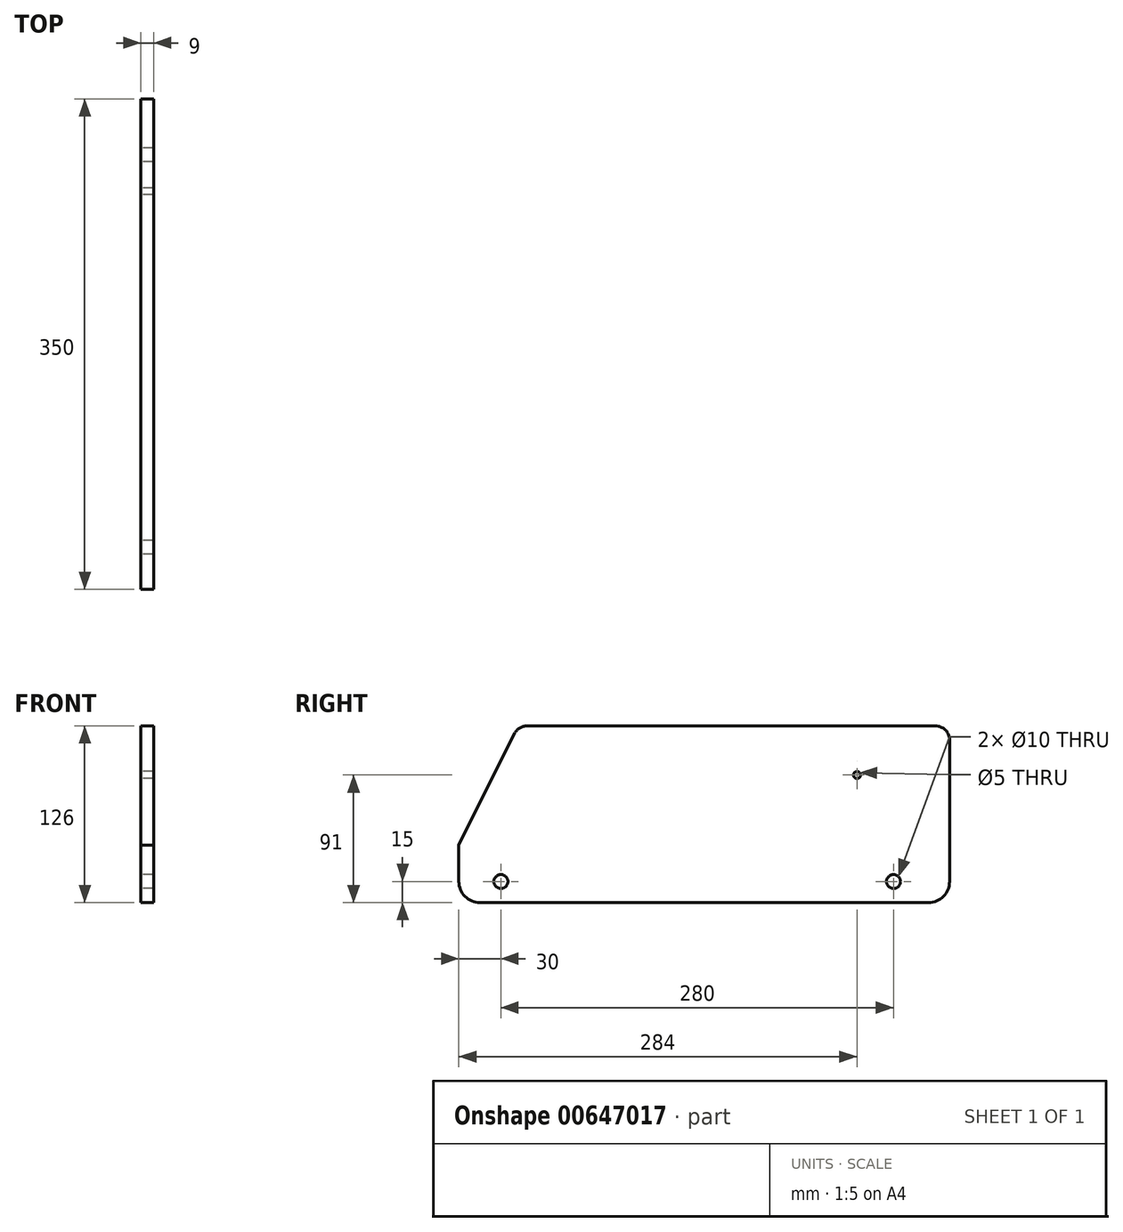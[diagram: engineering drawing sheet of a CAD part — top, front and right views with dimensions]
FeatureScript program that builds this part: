
annotation { "Feature Type Name" : "Feature", "Feature Type Description" : "" }
export const myFeature = defineFeature(function(context is Context, id is Id, definition is map)
    precondition{}
    {
        {
            var Q0;
            Q0=qCreatedBy(makeId("Right.planeOp"),FACE);
            var sketch = newSketch(context, id + "F0", { "sketchPlane" : qUnion([Q0])});
            skLineSegment(sketch, "E0.top", {"start": v(165, 101) * mm, "end": v(-126.39, 101) * mm});
            skLineSegment(sketch, "E0.left", {"start": v(175, -10) * mm, "end": v(175, 91) * mm});
            skLineSegment(sketch, "E0.right", {"start": v(-175, -10) * mm, "end": v(-175, 16) * mm});
            skPoint(sketch, "E0.middle", {"position": v(0, 50.5) * mm});
            skPoint(sketch, "E1.visualSharp", {"position": v(-175, 101) * mm});
            skArc(sketch, "E2.filletArc", {"start": v(175, 91) * mm, "mid": v(172.07, 98.07) * mm, "end": v(165, 101) * mm});
            skPoint(sketch, "E3.visualSharp", {"position": v(175, 0) * mm});
            skArc(sketch, "E3.filletArc", {"start": v(160, -25) * mm, "mid": v(170.6, -20.6) * mm, "end": v(175, -10) * mm});
            skPoint(sketch, "E4.visualSharp", {"position": v(-175, -19) * mm});
            skArc(sketch, "E4.filletArc", {"start": v(-175, -10) * mm, "mid": v(-170.6, -20.6) * mm, "end": v(-160, -25) * mm});
            skLineSegment(sketch, "E5", {"start": v(-160, -25) * mm, "end": v(160, -25) * mm});
            skCircle(sketch, "E6", {"center": v(-145, -10) * mm, "radius": 5 * mm});
            skCircle(sketch, "E7", {"center": v(135, -10) * mm, "radius": 5 * mm});
            skLineSegment(sketch, "E8", {"start": v(-145, -10) * mm, "end": v(135, -10) * mm, "construction": true});
            skLineSegment(sketch, "E9.bottom", {"start": v(-175, 0) * mm, "end": v(125, 0) * mm, "construction": true});
            skLineSegment(sketch, "E9.top", {"start": v(-175, 16) * mm, "end": v(125, 16) * mm, "construction": true});
            skLineSegment(sketch, "E9.left", {"start": v(-175, 0) * mm, "end": v(-175, 16) * mm});
            skLineSegment(sketch, "E9.right", {"start": v(125, 0) * mm, "end": v(125, 16) * mm, "construction": true});
            skPoint(sketch, "E9.middle", {"position": v(-25, 8) * mm});
            skLineSegment(sketch, "E10", {"start": v(125, 0) * mm, "end": v(125, 66) * mm, "construction": true});
            skLineSegment(sketch, "E11", {"start": v(125, 66) * mm, "end": v(109, 66) * mm, "construction": true});
            skCircle(sketch, "E12", {"center": v(109, 66) * mm, "radius": 2.5 * mm});
            skCircle(sketch, "E13", {"center": v(109, 66) * mm, "radius": 16 * mm, "construction": true});
            skLineSegment(sketch, "E14", {"start": v(-135.34, 95.47) * mm, "end": v(-175, 16) * mm});
            skPoint(sketch, "E15.visualSharp", {"position": v(-132.57, 101) * mm});
            skArc(sketch, "E15.filletArc", {"start": v(-126.39, 101) * mm, "mid": v(-131.65, 99.5) * mm, "end": v(-135.34, 95.47) * mm});
            skSolve(sketch);
        }
        {
            var Q0;
            Q0=makeQuery(id+"F0.imprint","IMPRINT",FACE,{"disambiguationData":[TD([[makeQuery(id+"F0.imprint","IMPRINT",EDGE,{"derivedFrom":sQuery(id+"F0.wireOp",EDGE,"E0.top")}),1.0]])]});
            extrude(context, id + "F1", {"entities" : qUnion([Q0]), "depth" : 9 * mm, "offsetDistance" : 25 * mm});
        }
    });
